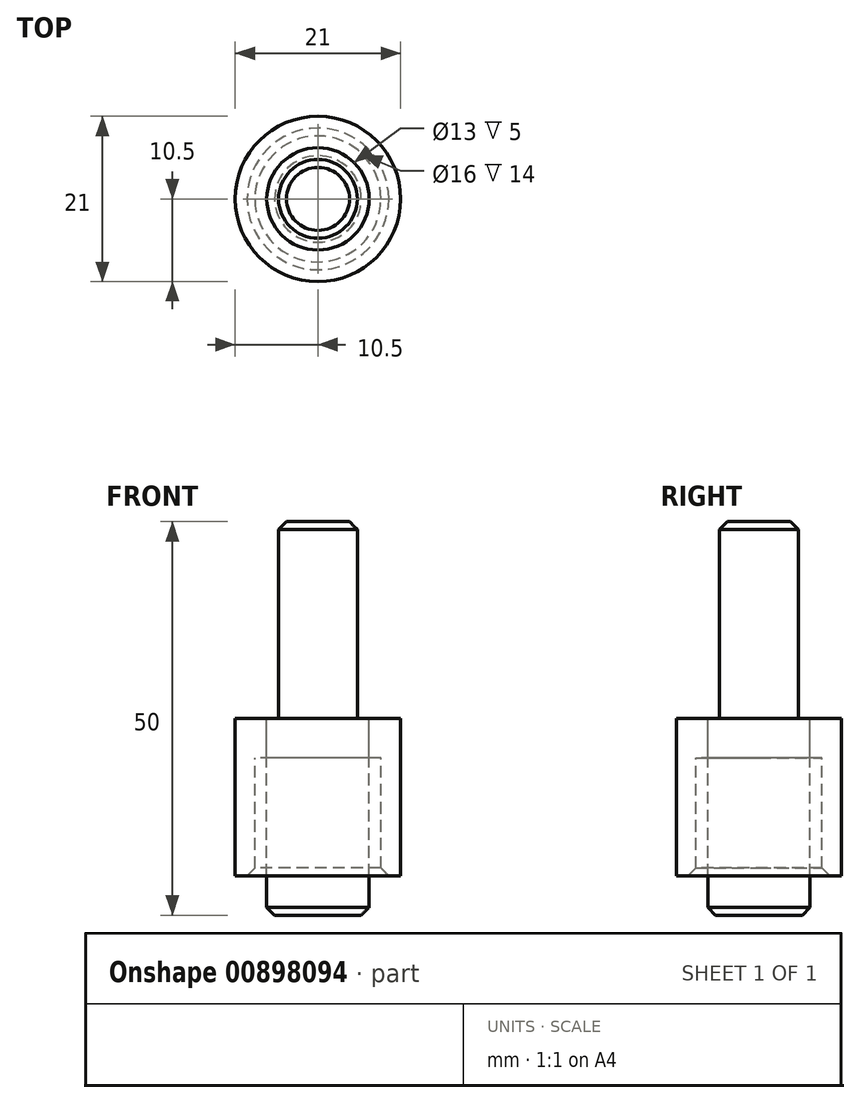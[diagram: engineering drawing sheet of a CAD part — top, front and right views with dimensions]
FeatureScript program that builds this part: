
annotation { "Feature Type Name" : "Feature", "Feature Type Description" : "" }
export const myFeature = defineFeature(function(context is Context, id is Id, definition is map)
    precondition{}
    {
        {
            var Q0;
            Q0=qCreatedBy(makeId("Top.planeOp"),FACE);
            var sketch = newSketch(context, id + "F0", { "sketchPlane" : qUnion([Q0])});
            skCircle(sketch, "E0", {"center": v(0, 0) * mm, "radius": 5 * mm});
            skCircle(sketch, "E1", {"center": v(0, 0) * mm, "radius": 6.5 * mm});
            skCircle(sketch, "E2", {"center": v(0, 0) * mm, "radius": 8 * mm});
            skCircle(sketch, "E3", {"center": v(0, 0) * mm, "radius": 10.5 * mm});
            skSolve(sketch);
        }
        {
            var Q0;
            Q0=makeQuery(id+"F0.imprint","IMPRINT",FACE,{"disambiguationData":[TD([[makeQuery(id+"F0.imprint","IMPRINT",EDGE,{"derivedFrom":sQuery(id+"F0.wireOp",EDGE,"E0")}),1.0]])]});
            extrude(context, id + "F1", {"entities" : qUnion([Q0]), "depth" : 25 * mm, "offsetDistance" : 25 * mm});
        }
        {
            var Q0;
            Q0=makeQuery(id+"F0.imprint","IMPRINT",FACE,{"disambiguationData":[TD([[makeQuery(id+"F0.imprint","IMPRINT",EDGE,{"derivedFrom":sQuery(id+"F0.wireOp",EDGE,"E0")}),1.0]])]});
            var Q1;
            Q1=makeQuery(id+"F0.imprint","IMPRINT",FACE,{"disambiguationData":[TD([[makeQuery(id+"F0.imprint","IMPRINT",EDGE,{"derivedFrom":sQuery(id+"F0.wireOp",EDGE,"E0")}),-1.0]])]});
            extrude(context, id + "F2", {"entities" : qUnion([Q0, Q1]), "operationType" : NewBodyOperationType.ADD, "oppositeDirection" : true, "depth" : 25 * mm, "offsetDistance" : 25 * mm});
        }
        {
            var Q0;
            Q0=makeQuery(id+"F0.imprint","IMPRINT",FACE,{"disambiguationData":[TD([[makeQuery(id+"F0.imprint","IMPRINT",EDGE,{"derivedFrom":sQuery(id+"F0.wireOp",EDGE,"E1")}),-1.0]])]});
            extrude(context, id + "F3", {"entities" : qUnion([Q0]), "oppositeDirection" : true, "depth" : 5 * mm, "offsetDistance" : 25 * mm});
        }
        {
            var Q0;
            Q0=makeQuery(id+"F0.imprint","IMPRINT",FACE,{"disambiguationData":[TD([[makeQuery(id+"F0.imprint","IMPRINT",EDGE,{"derivedFrom":sQuery(id+"F0.wireOp",EDGE,"E2")}),-1.0]])]});
            extrude(context, id + "F4", {"entities" : qUnion([Q0]), "operationType" : NewBodyOperationType.ADD, "oppositeDirection" : true, "depth" : 20 * mm, "offsetDistance" : 25 * mm});
        }
        {
            var Q0;
            Q0=makeQuery(id+"F4.opExtrude","CAP_EDGE",EDGE,{"disambiguationData":[OSD([sQuery(id+"F0.wireOp",EDGE,"E2")])],"isStart":false});
            var Q1;
            Q1=makeQuery(id+"F2.opExtrude","CAP_EDGE",EDGE,{"disambiguationData":[OSD([sQuery(id+"F0.wireOp",EDGE,"E1")])],"isStart":false});
            var Q2;
            Q2=makeQuery(id+"F1.opExtrude","CAP_EDGE",EDGE,{"disambiguationData":[OSD([sQuery(id+"F0.wireOp",EDGE,"E0")])],"isStart":false});
            chamfer(context, id + "F5", {"entities" : qUnion([Q0, Q1, Q2]), "width" : 1 * mm, "tangentPropagation" : true});
        }
    });
